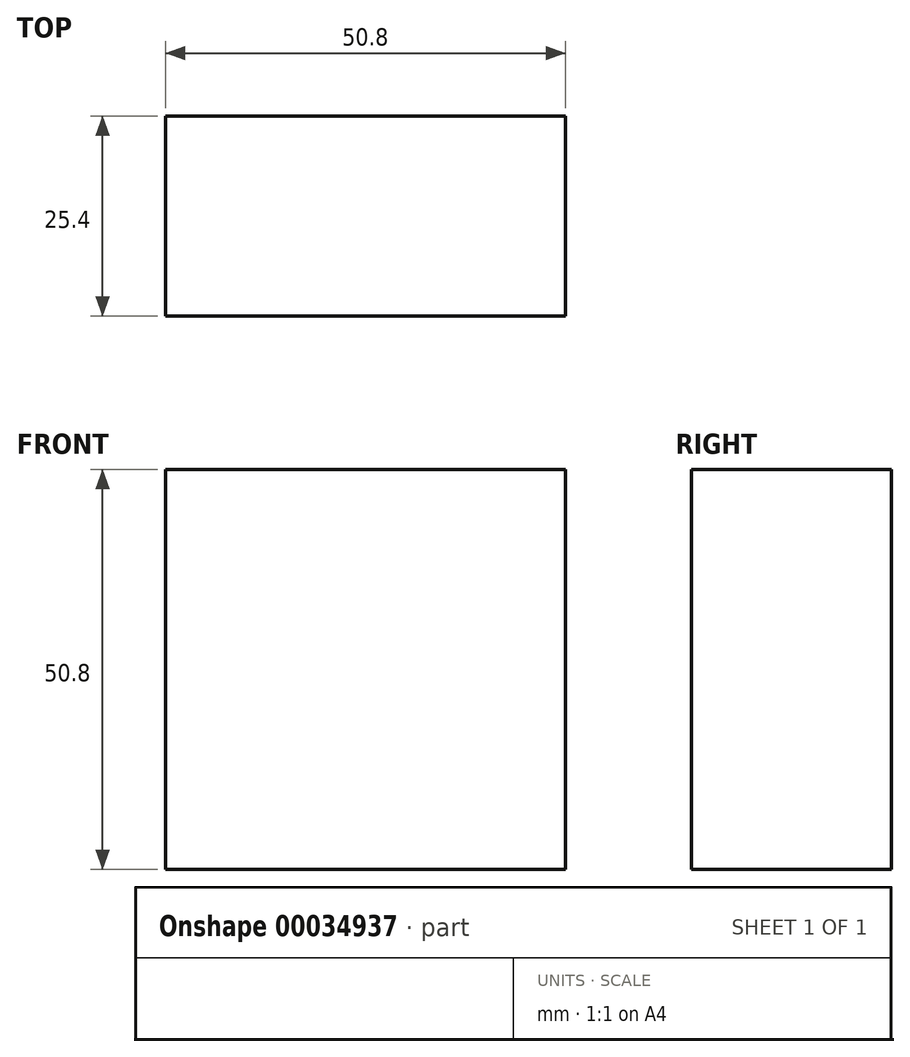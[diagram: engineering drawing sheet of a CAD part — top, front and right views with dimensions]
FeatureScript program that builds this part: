
annotation { "Feature Type Name" : "Feature", "Feature Type Description" : "" }
export const myFeature = defineFeature(function(context is Context, id is Id, definition is map)
    precondition{}
    {
        {
            var Q0;
            Q0=qCreatedBy(makeId("Front.planeOp"),FACE);
            var sketch = newSketch(context, id + "F0", { "sketchPlane" : qUnion([Q0])});
            skLineSegment(sketch, "E0.rect.bottom", {"start": v(25.4, 25.4) * mm, "end": v(-25.4, 25.4) * mm});
            skLineSegment(sketch, "E0.rect.top", {"start": v(25.4, -25.4) * mm, "end": v(-25.4, -25.4) * mm});
            skLineSegment(sketch, "E0.rect.left", {"start": v(25.4, 25.4) * mm, "end": v(25.4, -25.4) * mm});
            skLineSegment(sketch, "E0.rect.right", {"start": v(-25.4, 25.4) * mm, "end": v(-25.4, -25.4) * mm});
            skPoint(sketch, "E0.rect.middle", {"position": v(0, 0) * mm});
            skSolve(sketch);
        }
        {
            var Q0;
            Q0 = qSketchRegion(id + "F0", true);
            extrude(context, id + "F1", {"entities" : qUnion([Q0]), "depth" : 25.4 * mm});
        }
    });
